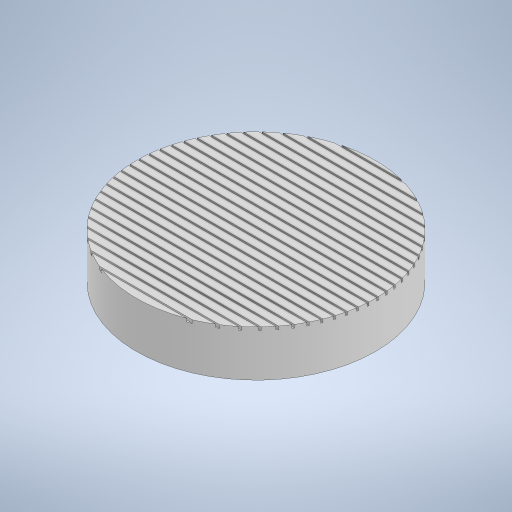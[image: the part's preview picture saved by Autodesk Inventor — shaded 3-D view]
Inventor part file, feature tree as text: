
AUTODESK INVENTOR PART (.ipt)
format: ipt  version: 2024 (Build 280153000, 153)  size: 404,480 bytes
history: native  units: mm
features: extrude x3
ambient origin geometry x8: Origin, YZ Plane, XZ Plane, XY Plane, X Axis, Y Axis, Z Axis, Center Point
bodies: Solid1 (feature_tree)
feature tree (3):
  extrude  "Extrusion1"  Depth=76.2mm
  extrude  "Extrusion2"  Depth=12.7mm TaperAngle=0.0deg
  extrude  "Extrusion3"  Depth=6.0mm
